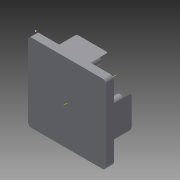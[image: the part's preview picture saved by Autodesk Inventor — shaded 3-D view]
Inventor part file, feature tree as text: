
AUTODESK INVENTOR PART (.ipt)
format: ipt  version: 2015 (Build 190159000, 159)  size: 183,808 bytes
history: native  units: mm
features: fillet x3, sketch x3, extrude x2, other x1, pattern_circular x1
ambient origin geometry x8: Origin, YZ Plane, XZ Plane, XY Plane, X Axis, Y Axis, Z Axis, Center Point
bodies: Solid1 (feature_tree)
feature tree (10):
  extrude  "Extrusion1"  Depth=20.0mm
  extrude  "Extrusion2"  Depth=4.0mm
  fillet  "Fillet1"  Radius=5.5mm
  fillet  "Fillet2"  Radius=1.8mm
  fillet  "Fillet3"  [1 undecoded]
  sketch  "Sketch3"  dims[d8=4.5mm d9=0.0mm d10=1.0mm d11=1.0mm d12=0.4mm d13=40.0mm d14=360.0deg]
  other  "Work Axis1"
  pattern_circular  "Circular Pattern1"  [2 undecoded]
  sketch  "Sketch1"  dims[d0=20.0mm d1=20.0mm]
  sketch  "Sketch2"  dims[d2=2.0mm d3=0.0mm d4=4.0mm d5=5.5mm d6=1.8mm d7=45.0deg]
note: 3 required parameter values undecoded (feature->parameter linkage not recoverable at this tier; creation-order binding heuristic only, values carry confidence <= 0.55)
